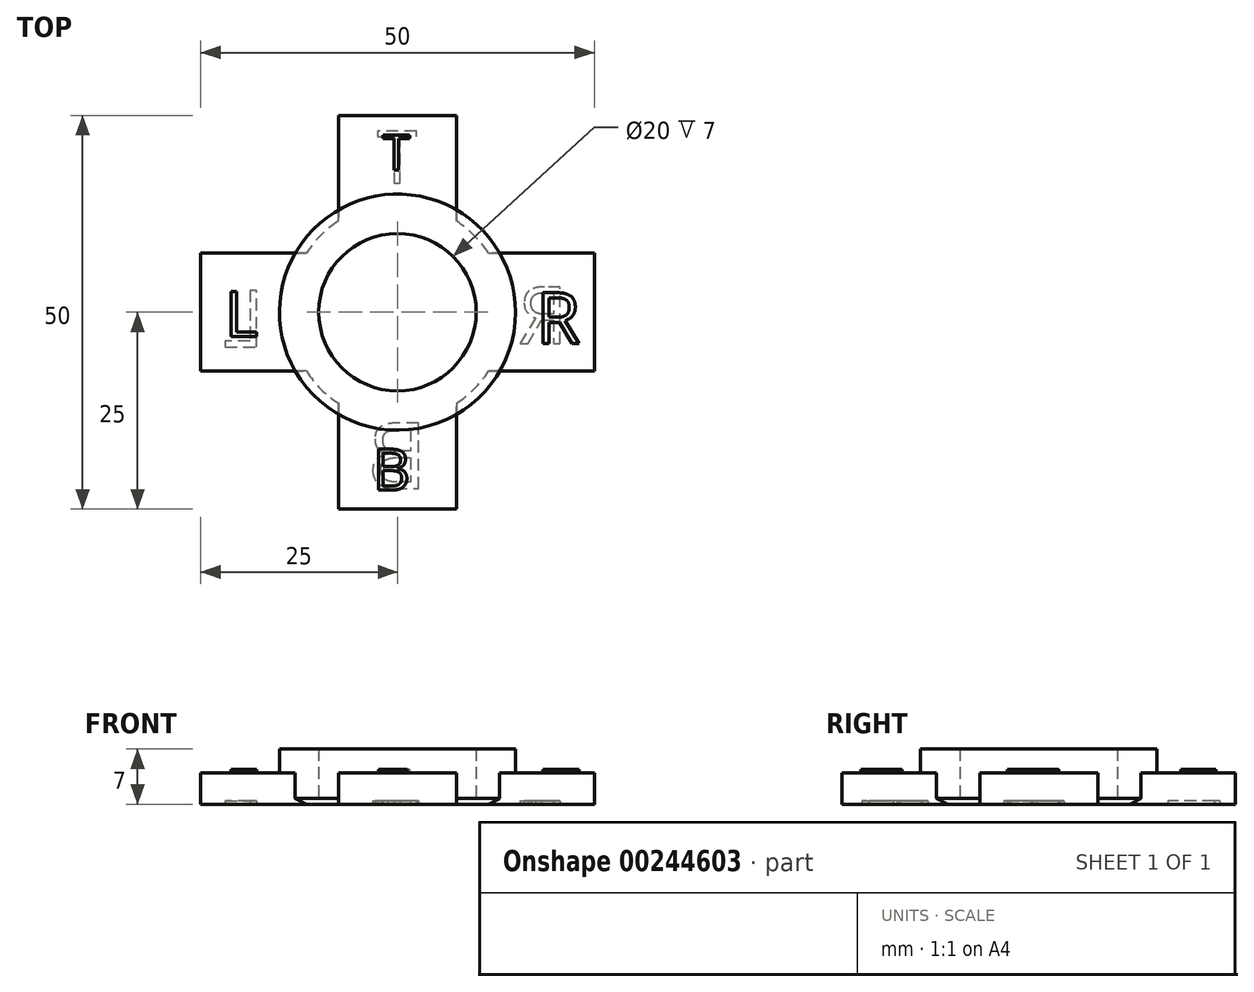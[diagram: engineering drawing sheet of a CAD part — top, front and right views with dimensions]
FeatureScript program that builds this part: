
annotation { "Feature Type Name" : "Feature", "Feature Type Description" : "" }
export const myFeature = defineFeature(function(context is Context, id is Id, definition is map)
    precondition{}
    {
        {
            var Q0;
            Q0=qCreatedBy(makeId("Top.planeOp"),FACE);
            var sketch = newSketch(context, id + "F0", { "sketchPlane" : qUnion([Q0])});
            skCircle(sketch, "E0", {"center": v(0, 0) * mm, "radius": 15 * mm});
            skCircle(sketch, "E1", {"center": v(0, 0) * mm, "radius": 10 * mm});
            skSolve(sketch);
        }
        {
            var Q0;
            Q0 = qSketchRegion(id + "F0", true);
            extrude(context, id + "F1", {"entities" : qUnion([Q0]), "depth" : 7 * mm});
        }
        {
            var Q0;
            Q0=makeQuery(id+"F1.opExtrude","CAP_FACE",FACE,{"disambiguationData":[OSD([sQuery(id+"F0.wireOp",EDGE,"E0"),sQuery(id+"F0.wireOp",EDGE,"E1")])],"isStart":true});
            var sketch = newSketch(context, id + "F2", { "sketchPlane" : qUnion([Q0])});
            skLineSegment(sketch, "E2", {"start": v(-7.5, 13) * mm, "end": v(-7.5, 25) * mm});
            skLineSegment(sketch, "E3", {"start": v(-7.5, 25) * mm, "end": v(7.5, 25) * mm});
            skLineSegment(sketch, "E4", {"start": v(7.5, 25) * mm, "end": v(7.5, 13) * mm});
            skArc(sketch, "E5", {"start": v(7.5, 13) * mm, "mid": v(0, 15) * mm, "end": v(-7.5, 13) * mm});
            skLineSegment(sketch, "E6.1.0", {"start": v(-25, -7.5) * mm, "end": v(-25, 7.5) * mm});
            skLineSegment(sketch, "E6.1.1", {"start": v(-13, -7.5) * mm, "end": v(-25, -7.5) * mm});
            skLineSegment(sketch, "E6.1.2", {"start": v(-25, 7.5) * mm, "end": v(-13, 7.5) * mm});
            skArc(sketch, "E6.1.3", {"start": v(-13, 7.5) * mm, "mid": v(-15, 0) * mm, "end": v(-13, -7.5) * mm});
            skLineSegment(sketch, "E6.2.0", {"start": v(7.5, -25) * mm, "end": v(-7.5, -25) * mm});
            skLineSegment(sketch, "E6.2.1", {"start": v(7.5, -13) * mm, "end": v(7.5, -25) * mm});
            skLineSegment(sketch, "E6.2.2", {"start": v(-7.5, -25) * mm, "end": v(-7.5, -13) * mm});
            skArc(sketch, "E6.2.3", {"start": v(-7.5, -13) * mm, "mid": v(0, -15) * mm, "end": v(7.5, -13) * mm});
            skLineSegment(sketch, "E6.3.0", {"start": v(25, 7.5) * mm, "end": v(25, -7.5) * mm});
            skLineSegment(sketch, "E6.3.1", {"start": v(13, 7.5) * mm, "end": v(25, 7.5) * mm});
            skLineSegment(sketch, "E6.3.2", {"start": v(25, -7.5) * mm, "end": v(13, -7.5) * mm});
            skArc(sketch, "E6.3.3", {"start": v(13, -7.5) * mm, "mid": v(15, 0) * mm, "end": v(13, 7.5) * mm});
            skSolve(sketch);
        }
        {
            var Q0;
            Q0 = qSketchRegion(id + "F2", true);
            extrude(context, id + "F3", {"entities" : qUnion([Q0]), "operationType" : NewBodyOperationType.ADD, "oppositeDirection" : true, "depth" : 4 * mm});
        }
        {
            var Q0;
            Q0=makeQuery(id+"F3.opExtrude","CAP_FACE",FACE,{"disambiguationData":[OSD([sQuery(id+"F2.wireOp",EDGE,"E6.2.0"),sQuery(id+"F2.wireOp",EDGE,"E6.2.1"),sQuery(id+"F2.wireOp",EDGE,"E6.2.2"),sQuery(id+"F2.wireOp",EDGE,"E6.2.3")])],"isStart":false});
            var sketch = newSketch(context, id + "F4", { "sketchPlane" : qUnion([Q0])});
            skText(sketch, "E7", { "text": "R", "fontName": "OpenSans-Regular.ttf"});
            skText(sketch, "E8", { "text": "L", "fontName": "OpenSans-Regular.ttf"});
            skText(sketch, "E9", { "text": "B", "fontName": "OpenSans-Regular.ttf"});
            skText(sketch, "E10", { "text": "T", "fontName": "OpenSans-Regular.ttf"});
            const initialGuessF4  = {"E7": [0.01762, -0.00397, 1, 0, 0.0065], "E8": [-0.02189, -0.0031, 1, 0, 0.00575], "E9": [-0.00313, -0.0226, 1, 0, 0.00525], "E10": [-0.00188, 0.01804, 1, 0, 0.0045]};
            skSetInitialGuess(sketch, initialGuessF4);
            skSolve(sketch);
        }
        {
            var Q0;
            Q0 = qSketchRegion(id + "F4", true);
            var Q1;
            Q1 = qConstructionFilter(qBodyType(qCreatedBy(id + "F4" ,EDGE), BodyType.WIRE), ConstructionObject.NO);
            extrude(context, id + "F5", {"entities" : qUnion([Q0]), "operationType" : NewBodyOperationType.ADD, "surfaceEntities" : qUnion([Q1]), "depth" : .4 * mm});
        }
        {
            var Q0;
            Q0=makeQuery(id+"F3.boolean.opBoolean","MERGE",FACE,{"derivedFrom":[makeQuery(id+"F1.opExtrude","CAP_FACE",FACE,{"disambiguationData":[OSD([sQuery(id+"F0.wireOp",EDGE,"E0"),sQuery(id+"F0.wireOp",EDGE,"E1")])],"isStart":true}),makeQuery(id+"F3.opExtrude","CAP_FACE",FACE,{"disambiguationData":[OSD([sQuery(id+"F2.wireOp",EDGE,"E2"),sQuery(id+"F2.wireOp",EDGE,"E3"),sQuery(id+"F2.wireOp",EDGE,"E4"),sQuery(id+"F2.wireOp",EDGE,"E5")])],"isStart":true}),makeQuery(id+"F3.opExtrude","CAP_FACE",FACE,{"disambiguationData":[OSD([sQuery(id+"F2.wireOp",EDGE,"E6.1.0"),sQuery(id+"F2.wireOp",EDGE,"E6.1.1"),sQuery(id+"F2.wireOp",EDGE,"E6.1.2"),sQuery(id+"F2.wireOp",EDGE,"E6.1.3")])],"isStart":true}),makeQuery(id+"F3.opExtrude","CAP_FACE",FACE,{"disambiguationData":[OSD([sQuery(id+"F2.wireOp",EDGE,"E6.2.0"),sQuery(id+"F2.wireOp",EDGE,"E6.2.1"),sQuery(id+"F2.wireOp",EDGE,"E6.2.2"),sQuery(id+"F2.wireOp",EDGE,"E6.2.3")])],"isStart":true}),makeQuery(id+"F3.opExtrude","CAP_FACE",FACE,{"disambiguationData":[OSD([sQuery(id+"F2.wireOp",EDGE,"E6.3.0"),sQuery(id+"F2.wireOp",EDGE,"E6.3.1"),sQuery(id+"F2.wireOp",EDGE,"E6.3.2"),sQuery(id+"F2.wireOp",EDGE,"E6.3.3")])],"isStart":true})]});
            var sketch = newSketch(context, id + "F6", { "sketchPlane" : qUnion([Q0])});
            skText(sketch, "E11", { "text": "T", "fontName": "OpenSans-Regular.ttf"});
            skText(sketch, "E12", { "text": "L", "fontName": "OpenSans-Regular.ttf"});
            skText(sketch, "E13", { "text": "R", "fontName": "OpenSans-Regular.ttf"});
            skText(sketch, "E14", { "text": "B", "fontName": "OpenSans-Regular.ttf"});
            const initialGuessF6  = {"E11": [0.00247, -0.0164, -1, 0, 0.00664], "E12": [-0.01693, 0.0044, -1, 0, 0.00722], "E13": [0.02165, 0.00398, -1, 0, 0.00726], "E14": [0.0038, 0.02243, -1, 0, 0.00844]};
            skSetInitialGuess(sketch, initialGuessF6);
            skSolve(sketch);
        }
        {
            var Q0;
            Q0 = qSketchRegion(id + "F6", true);
            extrude(context, id + "F7", {"entities" : qUnion([Q0]), "operationType" : NewBodyOperationType.REMOVE, "oppositeDirection" : true, "depth" : .4 * mm});
        }
        {
            var Q0;
            {var subQ0=sQuery(id+"F2.wireOp",EDGE,"E4");var subQ2=sQuery(id+"F0.wireOp",EDGE,"E0");Q0=makeQuery(id+"F3.boolean.opBoolean","SPLIT",EDGE,{"disambiguationData":[TD([makeQuery(id+"F3.opExtrude","SWEPT_FACE",FACE,{"disambiguationData":[OSD([subQ0])]})])],"derivedFrom":makeQuery(id+"F1.opExtrude","CAP_EDGE",EDGE,{"disambiguationData":[OSD([subQ2])],"isStart":true})});}
            var Q1;
            {var subQ0=sQuery(id+"F0.wireOp",EDGE,"E0");var subQ1=sQuery(id+"F2.wireOp",EDGE,"E6.2.1");Q1=makeQuery(id+"F3.boolean.opBoolean","SPLIT",EDGE,{"disambiguationData":[TD([makeQuery(id+"F3.opExtrude","SWEPT_FACE",FACE,{"disambiguationData":[OSD([subQ1])]})])],"derivedFrom":makeQuery(id+"F1.opExtrude","CAP_EDGE",EDGE,{"disambiguationData":[OSD([subQ0])],"isStart":true})});}
            var Q2;
            {var subQ0=sQuery(id+"F2.wireOp",EDGE,"E6.1.1");var subQ1=sQuery(id+"F0.wireOp",EDGE,"E0");Q2=makeQuery(id+"F3.boolean.opBoolean","SPLIT",EDGE,{"disambiguationData":[TD([makeQuery(id+"F3.opExtrude","SWEPT_FACE",FACE,{"disambiguationData":[OSD([subQ0])]})])],"derivedFrom":makeQuery(id+"F1.opExtrude","CAP_EDGE",EDGE,{"disambiguationData":[OSD([subQ1])],"isStart":true})});}
            var Q3;
            {var subQ0=sQuery(id+"F2.wireOp",EDGE,"E2");var subQ1=sQuery(id+"F0.wireOp",EDGE,"E0");Q3=makeQuery(id+"F3.boolean.opBoolean","SPLIT",EDGE,{"disambiguationData":[TD([makeQuery(id+"F3.opExtrude","SWEPT_FACE",FACE,{"disambiguationData":[OSD([subQ0])]})])],"derivedFrom":makeQuery(id+"F1.opExtrude","CAP_EDGE",EDGE,{"disambiguationData":[OSD([subQ1])],"isStart":true})});}
            chamfer(context, id + "F8", {"entities" : qUnion([Q0, Q1, Q2, Q3]), "chamferType" : ChamferType.OFFSET_ANGLE, "width" : .7 * mm, "oppositeDirection" : false, "angle" : 60 * degree, "tangentPropagation" : true});
        }
    });
